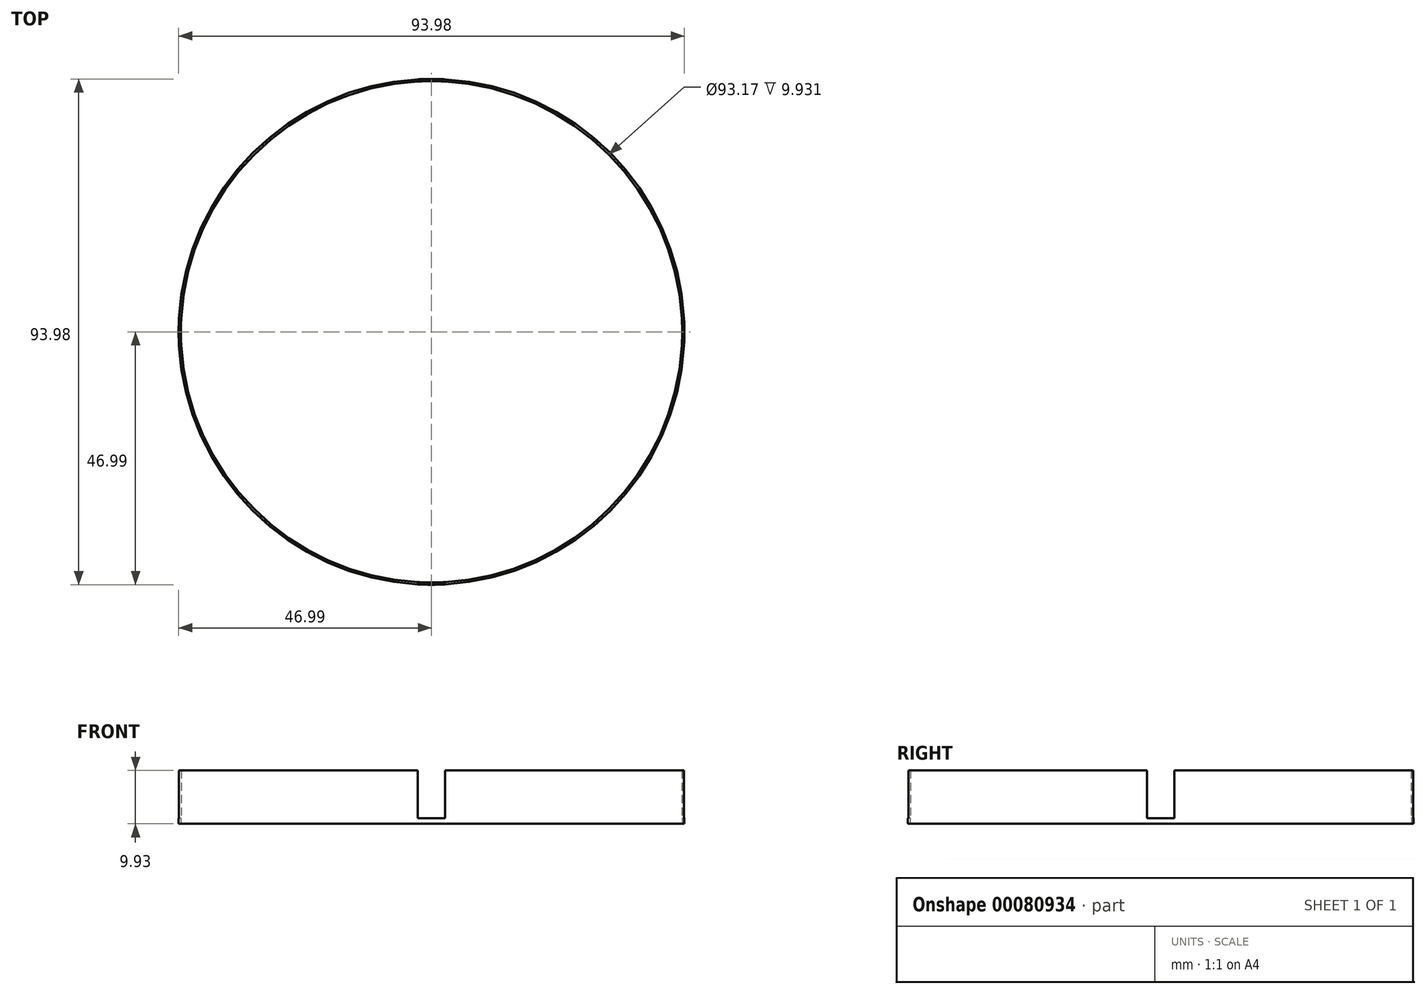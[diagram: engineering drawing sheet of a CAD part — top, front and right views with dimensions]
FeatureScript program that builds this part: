
annotation { "Feature Type Name" : "Feature", "Feature Type Description" : "" }
export const myFeature = defineFeature(function(context is Context, id is Id, definition is map)
    precondition{}
    {
        {
            var Q0;
            Q0=qCreatedBy(makeId("Top.planeOp"),FACE);
            var sketch = newSketch(context, id + "F0", { "sketchPlane" : qUnion([Q0])});
            skCircle(sketch, "E0", {"center": v(0, 0) * mm, "radius": 47 * mm});
            skCircle(sketch, "E1", {"center": v(0, 0) * mm, "radius": 46.58 * mm});
            skSolve(sketch);
        }
        {
            var Q0;
            Q0=makeQuery(id+"F0.imprint","IMPRINT",FACE,{"disambiguationData":[TD([[makeQuery(id+"F0.imprint","IMPRINT",EDGE,{"derivedFrom":sQuery(id+"F0.wireOp",EDGE,"E0")}),1.0]])]});
            extrude(context, id + "F1", {"entities" : qUnion([Q0]), "depth" : 9.93 * mm});
        }
        {
            var Q0;
            Q0=qCreatedBy(makeId("Right.planeOp"),FACE);
            var sketch = newSketch(context, id + "F2", { "sketchPlane" : qUnion([Q0])});
            skLineSegment(sketch, "E2.bottom", {"start": v(-2.54, 1.05) * mm, "end": v(2.54, 1.05) * mm});
            skLineSegment(sketch, "E2.top", {"start": v(-2.54, 13.75) * mm, "end": v(2.54, 13.75) * mm});
            skLineSegment(sketch, "E2.left", {"start": v(-2.54, 1.05) * mm, "end": v(-2.54, 13.75) * mm});
            skLineSegment(sketch, "E2.right", {"start": v(2.54, 1.05) * mm, "end": v(2.54, 13.75) * mm});
            skSolve(sketch);
        }
        {
            var Q0;
            Q0=makeQuery(id+"F2.imprint","IMPRINT",FACE,{"disambiguationData":[TD([[makeQuery(id+"F2.imprint","IMPRINT",EDGE,{"derivedFrom":sQuery(id+"F2.wireOp",EDGE,"E2.bottom")}),1.0]])]});
            extrude(context, id + "F3", {"entities" : qUnion([Q0]), "operationType" : NewBodyOperationType.REMOVE, "oppositeDirection" : true, "depth" : 152.4 * mm, "symmetric" : true});
        }
        {
            var Q0;
            Q0=qCreatedBy(makeId("Front.planeOp"),FACE);
            var sketch = newSketch(context, id + "F4", { "sketchPlane" : qUnion([Q0])});
            skLineSegment(sketch, "E3.bottom", {"start": v(-2.54, 1.05) * mm, "end": v(2.54, 1.05) * mm});
            skLineSegment(sketch, "E3.top", {"start": v(-2.54, 13.75) * mm, "end": v(2.54, 13.75) * mm});
            skLineSegment(sketch, "E3.left", {"start": v(-2.54, 1.05) * mm, "end": v(-2.54, 13.75) * mm});
            skLineSegment(sketch, "E3.right", {"start": v(2.54, 1.05) * mm, "end": v(2.54, 13.75) * mm});
            skSolve(sketch);
        }
        {
            var Q0;
            Q0=makeQuery(id+"F4.imprint","IMPRINT",FACE,{"disambiguationData":[TD([[makeQuery(id+"F4.imprint","IMPRINT",EDGE,{"derivedFrom":sQuery(id+"F4.wireOp",EDGE,"E3.bottom")}),1.0]])]});
            extrude(context, id + "F5", {"entities" : qUnion([Q0]), "operationType" : NewBodyOperationType.REMOVE, "oppositeDirection" : true, "depth" : 152.4 * mm, "symmetric" : true});
        }
    });
